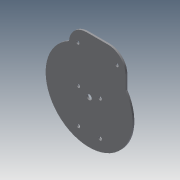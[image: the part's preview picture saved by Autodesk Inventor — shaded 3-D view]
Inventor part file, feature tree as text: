
AUTODESK INVENTOR PART (.ipt)
format: ipt  version: 2013 (Build 170138000, 138)  size: 166,912 bytes
history: native  units: mm
features: sketch x12, extrude x10, fillet x1
ambient origin geometry x8: Origin, YZ Plane, XZ Plane, XY Plane, X Axis, Y Axis, Z Axis, Center Point
bodies: Solid1 (feature_tree)
feature tree (23):
  extrude  "Extrusion1"  Depth=6.0mm
  extrude  "Extrusion2"  Depth=23.0mm
  extrude  "Extrusion3"  Depth=4.0mm
  extrude  "Extrusion4"  Depth=4.0mm
  extrude  "Extrusion5"  Depth=2.0mm TaperAngle=0.0deg
  extrude  "Extrusion6"  Depth=27.5mm
  extrude  "Extrusion7"  Depth=4.0mm
  fillet  "Fillet1"  Radius=4.0mm
  sketch  "Sketch8"  dims[d29=4.0mm d30=2.0mm d31=0.0mm]
  extrude  "Extrusion8"  Depth=2.0mm TaperAngle=0.0deg
  extrude  "Extrusion9"  Depth=41.9mm
  extrude  "Extrusion10"  Depth=2.0mm TaperAngle=0.0deg
  sketch  "Sketch12"  dims[d38=10.0mm d39=15.3mm d40=10.0mm d41=15.3mm d42=4.0mm d43=4.0mm d44=2.0mm d45=0.0mm d46=20.0mm d50=2.0mm d51=0.0mm d55=4.0mm d56=4.0mm d59=4.0mm d60=4.0mm d61=2.0mm d62=0.0mm d63=6.0mm d64=2.0mm d65=0.0mm]
  sketch  "Sketch1"  dims[d1=2.0mm d2=0.0mm d3=6.0mm]
  sketch  "Sketch2"  dims[d4=2.0mm d5=0.0mm d15=23.0mm]
  sketch  "Sketch3"  dims[d16=40.0mm d17=4.0mm]
  sketch  "Sketch4"  dims[d18=4.0mm d19=4.0mm]
  sketch  "Sketch5"  dims[d20=4.0mm d21=2.0mm d22=0.0mm]
  sketch  "Sketch6"  dims[d23=2.0mm d24=0.0mm d25=27.5mm]
  sketch  "Sketch7"  dims[d26=4.0mm d27=4.0mm d28=4.0mm]
  sketch  "Sketch9"  dims[d32=63.2mm d33=41.9mm]
  sketch  "Sketch10"  dims[d34=23.1mm d35=2.0mm d36=0.0mm]
  sketch  "Sketch11"  dims[d37=30.6mm]
